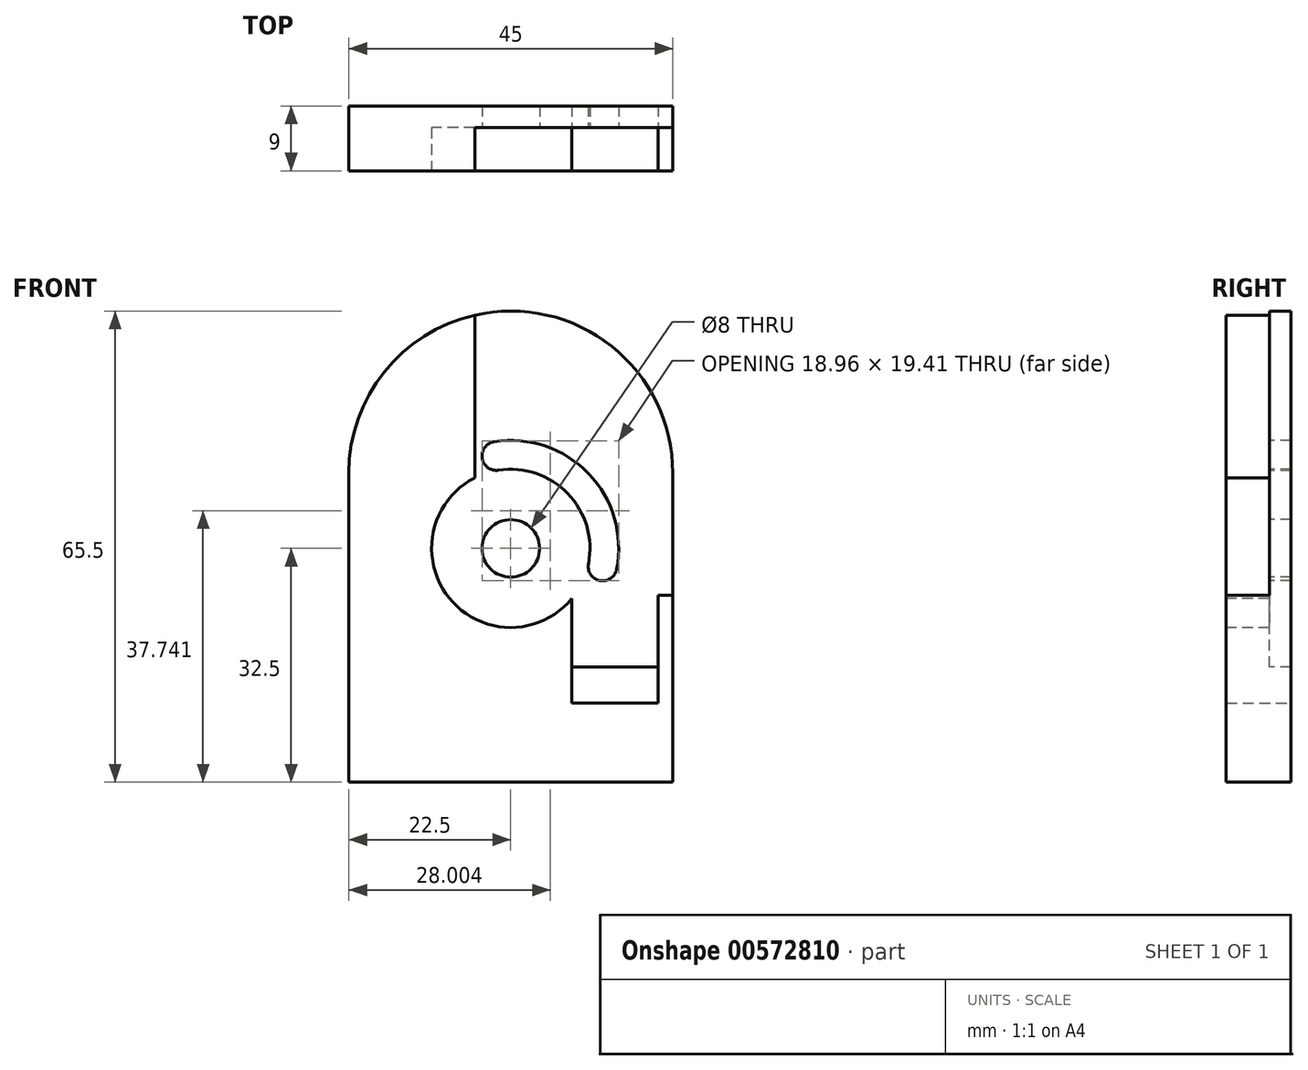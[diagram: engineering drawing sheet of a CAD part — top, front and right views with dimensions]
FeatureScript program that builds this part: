
annotation { "Feature Type Name" : "Feature", "Feature Type Description" : "" }
export const myFeature = defineFeature(function(context is Context, id is Id, definition is map)
    precondition{}
    {
        {
            var Q0;
            Q0=qCreatedBy(makeId("Front.planeOp"),FACE);
            var sketch = newSketch(context, id + "F0", { "sketchPlane" : qUnion([Q0])});
            skLineSegment(sketch, "E0.bottom", {"start": v(-22.5, 21.5) * mm, "end": v(22.5, 21.5) * mm});
            skLineSegment(sketch, "E0.top", {"start": v(-22.5, -21.5) * mm, "end": v(22.5, -21.5) * mm});
            skLineSegment(sketch, "E0.left", {"start": v(-22.5, 21.5) * mm, "end": v(-22.5, -21.5) * mm});
            skLineSegment(sketch, "E0.right", {"start": v(22.5, 21.5) * mm, "end": v(22.5, -21.5) * mm});
            skPoint(sketch, "E0.middle", {"position": v(0, 0) * mm});
            skLineSegment(sketch, "E1", {"start": v(0, 21.5) * mm, "end": v(0, 44) * mm});
            skPoint(sketch, "E1.endSnap0", {"position": v(0, 21.5) * mm});
            skCircle(sketch, "E2", {"center": v(0, 21.5) * mm, "radius": 22.5 * mm});
            skLineSegment(sketch, "E3", {"start": v(0, 44) * mm, "end": v(0, -21.5) * mm});
            skSolve(sketch);
        }
        {
            var Q0;
            Q0 = qSketchRegion(id + "F0", true);
            extrude(context, id + "F1", {"entities" : qUnion([Q0]), "depth" : 9 * mm, "offsetDistance" : 25 * mm});
        }
        {
            var Q0;
            Q0=makeQuery(id+"F1.opExtrude","CAP_FACE",FACE,{"disambiguationData":[OSD([sQuery(id+"F0.wireOp",EDGE,"E0.top"),sQuery(id+"F0.wireOp",EDGE,"E0.left"),sQuery(id+"F0.wireOp",EDGE,"E0.right"),sQuery(id+"F0.wireOp",EDGE,"E2")])],"isStart":false});
            var sketch = newSketch(context, id + "F2", { "sketchPlane" : qUnion([Q0])});
            skLineSegment(sketch, "E4", {"start": v(0, 44) * mm, "end": v(0, 11) * mm});
            skCircle(sketch, "E5", {"center": v(0, 11) * mm, "radius": 11 * mm});
            skLineSegment(sketch, "E6", {"start": v(0, 30.82) * mm, "end": v(-5, 30.82) * mm});
            skLineSegment(sketch, "E7", {"start": v(-5, 30.82) * mm, "end": v(-5, 14.18) * mm});
            skLineSegment(sketch, "E8", {"start": v(-5, 14.18) * mm, "end": v(-5, 43.44) * mm});
            skLineSegment(sketch, "E9", {"start": v(22.5, -21.5) * mm, "end": v(22.5, 4.5) * mm});
            skLineSegment(sketch, "E10", {"start": v(22.5, 4.5) * mm, "end": v(8.87, 4.5) * mm});
            skSolve(sketch);
        }
        {
            var Q0;
            {var subQ3=sQuery(id+"F2.wireOp",EDGE,"E6");Q0=makeQuery(id+"F2.imprint","IMPRINT",FACE,{"disambiguationData":[TD([[makeQuery(id+"F2.imprint","IMPRINT",EDGE,{"derivedFrom":subQ3}),-1.0]])]});}
            var Q1;
            {var subQ0=sQuery(id+"F2.wireOp",EDGE,"E6");Q1=makeQuery(id+"F2.imprint","IMPRINT",FACE,{"disambiguationData":[TD([[makeQuery(id+"F2.imprint","IMPRINT",EDGE,{"derivedFrom":subQ0}),1.0]])]});}
            var Q2;
            {var subQ0=sQuery(id+"F2.wireOp",EDGE,"E5");var subQ1=makeQuery(id+"F2.imprint","INTERSECT",VERTEX,{"derivedFrom":[sQuery(id+"F2.wireOp",EDGE,"E4"),subQ0]});Q2=makeQuery(id+"F2.imprint","IMPRINT",FACE,{"disambiguationData":[TD([[makeQuery(id+"F2.imprint","IMPRINT",EDGE,{"disambiguationData":[TD([[subQ1,-1.0]])],"derivedFrom":subQ0}),1.0]])]});}
            var Q3;
            {var subQ0=sQuery(id+"F2.wireOp",EDGE,"E10");Q3=makeQuery(id+"F2.imprint","IMPRINT",FACE,{"disambiguationData":[TD([[makeQuery(id+"F2.imprint","IMPRINT",EDGE,{"derivedFrom":subQ0}),-1.0]])]});}
            extrude(context, id + "F3", {"entities" : qUnion([Q0, Q1, Q2, Q3]), "operationType" : NewBodyOperationType.REMOVE, "oppositeDirection" : true, "depth" : 6 * mm, "offsetDistance" : 25 * mm});
        }
        {
            var Q0;
            Q0=makeQuery(id+"F3.boolean.opBoolean","COPY",FACE,{"derivedFrom":makeQuery(id+"F3.opExtrude","CAP_FACE",FACE,{"disambiguationData":[OSD([sQuery(id+"F0.wireOp",EDGE,"E0.right"),sQuery(id+"F0.wireOp",EDGE,"E2"),sQuery(id+"F2.wireOp",EDGE,"E5"),sQuery(id+"F2.wireOp",EDGE,"E8"),sQuery(id+"F2.wireOp",EDGE,"E10")])],"isStart":false})});
            var sketch = newSketch(context, id + "F4", { "sketchPlane" : qUnion([Q0])});
            skCircle(sketch, "E11", {"center": v(0, 11) * mm, "radius": 4 * mm});
            skCircle(sketch, "E12", {"center": v(0, 11) * mm, "radius": 11 * mm});
            skCircle(sketch, "E13", {"center": v(0, 11) * mm, "radius": 15 * mm});
            skLineSegment(sketch, "E14", {"start": v(18.24, 4.5) * mm, "end": v(18.24, 6.5) * mm});
            skLineSegment(sketch, "E15", {"start": v(18.24, 6.5) * mm, "end": v(10.04, 6.5) * mm});
            skLineSegment(sketch, "E16", {"start": v(-5, 34.14) * mm, "end": v(-4, 34.14) * mm});
            skLineSegment(sketch, "E17", {"start": v(-4, 34.14) * mm, "end": v(-4, 21.25) * mm});
            skSolve(sketch);
        }
        {
            var Q0;
            {var subQ0=sQuery(id+"F4.wireOp",EDGE,"E15");var subQ1=sQuery(id+"F4.wireOp",EDGE,"E12");var subQ2=makeQuery(id+"F4.imprint","INTERSECT",VERTEX,{"derivedFrom":[subQ1,subQ0]});Q0=makeQuery(id+"F4.imprint","IMPRINT",FACE,{"disambiguationData":[TD([[makeQuery(id+"F4.imprint","IMPRINT",EDGE,{"disambiguationData":[TD([[subQ2,-1.0]])],"derivedFrom":subQ1}),-1.0]])]});}
            var Q1;
            Q1=makeQuery(id+"F4.imprint","IMPRINT",FACE,{"disambiguationData":[TD([[makeQuery(id+"F4.imprint","IMPRINT",EDGE,{"derivedFrom":sQuery(id+"F4.wireOp",EDGE,"E11")}),1.0]])]});
            extrude(context, id + "F5", {"entities" : qUnion([Q0, Q1]), "operationType" : NewBodyOperationType.REMOVE, "oppositeDirection" : true, "depth" : 25 * mm, "offsetDistance" : 25 * mm});
        }
        {
            var Q0;
            Q0=makeQuery(id+"F5.boolean.opBoolean","COPY",EDGE,{"derivedFrom":makeQuery(id+"F5.opExtrude","SWEPT_EDGE",EDGE,{"disambiguationData":[OSD([sQuery(id+"F4.wireOp",EDGE,"E13"),sQuery(id+"F4.wireOp",EDGE,"E17")])]})});
            var Q1;
            Q1=makeQuery(id+"F5.boolean.opBoolean","COPY",EDGE,{"derivedFrom":makeQuery(id+"F5.opExtrude","SWEPT_EDGE",EDGE,{"disambiguationData":[OSD([sQuery(id+"F4.wireOp",EDGE,"E12"),sQuery(id+"F4.wireOp",EDGE,"E17")])]})});
            var Q2;
            Q2=makeQuery(id+"F5.boolean.opBoolean","COPY",EDGE,{"derivedFrom":makeQuery(id+"F5.opExtrude","SWEPT_EDGE",EDGE,{"disambiguationData":[OSD([sQuery(id+"F4.wireOp",EDGE,"E13"),sQuery(id+"F4.wireOp",EDGE,"E15")])]})});
            var Q3;
            Q3=makeQuery(id+"F5.boolean.opBoolean","COPY",EDGE,{"derivedFrom":makeQuery(id+"F5.opExtrude","SWEPT_EDGE",EDGE,{"disambiguationData":[OSD([sQuery(id+"F4.wireOp",EDGE,"E12"),sQuery(id+"F4.wireOp",EDGE,"E15")])]})});
            fillet(context, id + "F6", {"entities" : qUnion([Q0, Q1, Q2, Q3]), "radius" : 2 * mm, "tangentPropagation" : true, "allowEdgeOverflow" : false});
        }
        {
            var Q0;
            Q0=makeQuery(id+"F3.boolean.opBoolean","COPY",FACE,{"derivedFrom":makeQuery(id+"F3.opExtrude","SWEPT_FACE",FACE,{"disambiguationData":[OSD([sQuery(id+"F2.wireOp",EDGE,"E10")])]})});
            var sketch = newSketch(context, id + "F7", { "sketchPlane" : qUnion([Q0])});
            skPoint(sketch, "E18.middle", {"position": v(15.69, -6) * mm});
            skPoint(sketch, "E18.middle.positionSnap0", {"position": v(8.87, -6) * mm});
            skPoint(sketch, "E18.middle.positionSnap1", {"position": v(15.69, -3) * mm});
            skPoint(sketch, "E18.centerSnap0", {"position": v(8.87, -6) * mm});
            skPoint(sketch, "E18.centerSnap1", {"position": v(15.69, -3) * mm});
            skLineSegment(sketch, "E19", {"start": v(22.5, -9) * mm, "end": v(20.5, -9) * mm});
            skLineSegment(sketch, "E20.bottom", {"start": v(20.5, -9) * mm, "end": v(8.5, -9) * mm});
            skLineSegment(sketch, "E20.top", {"start": v(20.5, -3) * mm, "end": v(8.5, -3) * mm});
            skLineSegment(sketch, "E20.left", {"start": v(20.5, -9) * mm, "end": v(20.5, -3) * mm});
            skLineSegment(sketch, "E20.right", {"start": v(8.5, -9) * mm, "end": v(8.5, -3) * mm});
            skSolve(sketch);
        }
        {
            var Q0;
            Q0 = qSketchRegion(id + "F7", true);
            extrude(context, id + "F8", {"entities" : qUnion([Q0]), "operationType" : NewBodyOperationType.REMOVE, "oppositeDirection" : true, "depth" : 15 * mm, "offsetDistance" : 25 * mm});
        }
        {
            var Q0;
            Q0=makeQuery(id+"F8.boolean.opBoolean","MERGE",FACE,{"derivedFrom":[makeQuery(id+"F3.boolean.opBoolean","COPY",FACE,{"derivedFrom":makeQuery(id+"F3.opExtrude","CAP_FACE",FACE,{"disambiguationData":[OSD([sQuery(id+"F0.wireOp",EDGE,"E0.right"),sQuery(id+"F0.wireOp",EDGE,"E2"),sQuery(id+"F2.wireOp",EDGE,"E5"),sQuery(id+"F2.wireOp",EDGE,"E8"),sQuery(id+"F2.wireOp",EDGE,"E10")])],"isStart":false})}),makeQuery(id+"F8.opExtrude","SWEPT_FACE",FACE,{"disambiguationData":[OSD([sQuery(id+"F7.wireOp",EDGE,"E18.bottom")])]})]});
            var sketch = newSketch(context, id + "F9", { "sketchPlane" : qUnion([Q0])});
            skLineSegment(sketch, "E21", {"start": v(20.5, 4.5) * mm, "end": v(20.5, -5.5) * mm});
            skLineSegment(sketch, "E22.bottom", {"start": v(20.5, -5.5) * mm, "end": v(20.5, -5.5) * mm});
            skLineSegment(sketch, "E22.top", {"start": v(20.5, -10.5) * mm, "end": v(20.5, -10.5) * mm});
            skLineSegment(sketch, "E22.left", {"start": v(20.5, -5.5) * mm, "end": v(20.5, -10.5) * mm});
            skLineSegment(sketch, "E22.right", {"start": v(20.5, -5.5) * mm, "end": v(20.5, -10.5) * mm});
            skLineSegment(sketch, "E23.bottom", {"start": v(20.5, -5.5) * mm, "end": v(8.5, -5.5) * mm});
            skLineSegment(sketch, "E23.top", {"start": v(20.5, -10.5) * mm, "end": v(8.5, -10.5) * mm});
            skLineSegment(sketch, "E23.right", {"start": v(8.5, -5.5) * mm, "end": v(8.5, -10.5) * mm});
            skSolve(sketch);
        }
        {
            var Q0;
            Q0 = qSketchRegion(id + "F9", true);
            extrude(context, id + "F10", {"entities" : qUnion([Q0]), "operationType" : NewBodyOperationType.REMOVE, "oppositeDirection" : true, "depth" : 25 * mm, "offsetDistance" : 25 * mm});
        }
    });
